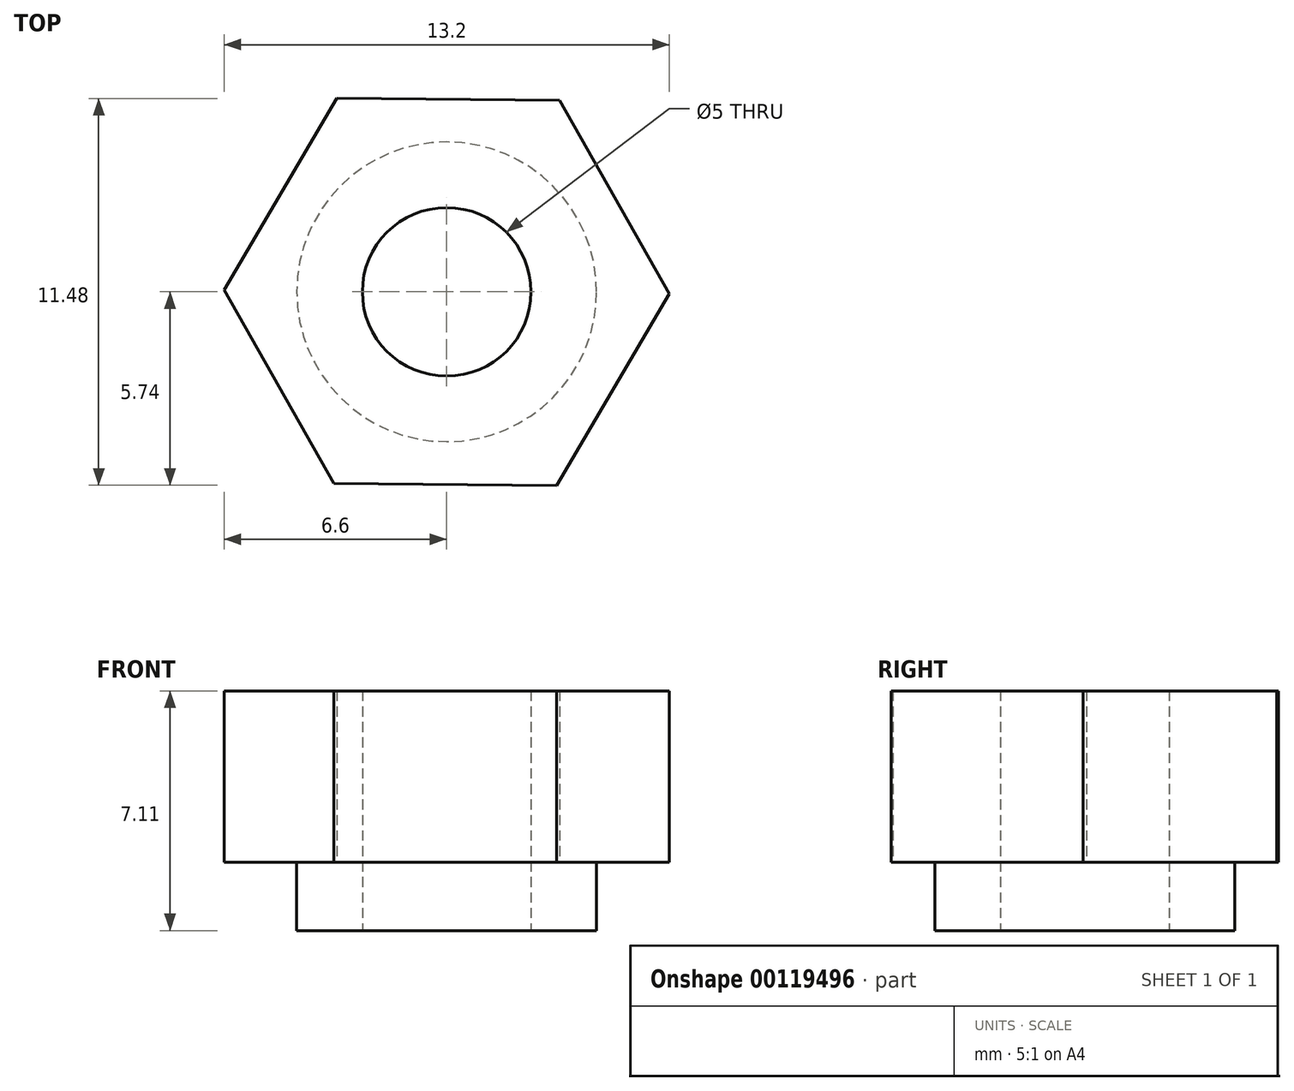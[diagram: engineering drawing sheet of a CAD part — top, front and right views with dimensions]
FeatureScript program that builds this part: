
annotation { "Feature Type Name" : "Feature", "Feature Type Description" : "" }
export const myFeature = defineFeature(function(context is Context, id is Id, definition is map)
    precondition{}
    {
        {
            var Q0;
            Q0=qCreatedBy(makeId("Top.planeOp"),FACE);
            var sketch = newSketch(context, id + "F0", { "sketchPlane" : qUnion([Q0])});
            skCircle(sketch, "E0.cCircle", {"center": v(0, 0) * mm, "radius": 6.6 * mm, "construction": true});
            skLineSegment(sketch, "E0.0", {"start": v(-3.25, 5.74) * mm, "end": v(3.35, 5.69) * mm});
            skLineSegment(sketch, "E0.1", {"start": v(3.35, 5.69) * mm, "end": v(6.6, -0.05) * mm});
            skLineSegment(sketch, "E0.2", {"start": v(6.6, -0.05) * mm, "end": v(3.25, -5.74) * mm});
            skLineSegment(sketch, "E0.3", {"start": v(3.25, -5.74) * mm, "end": v(-3.35, -5.69) * mm});
            skLineSegment(sketch, "E0.4", {"start": v(-3.35, -5.69) * mm, "end": v(-6.6, 0.05) * mm});
            skLineSegment(sketch, "E0.5", {"start": v(-6.6, 0.05) * mm, "end": v(-3.25, 5.74) * mm});
            skSolve(sketch);
        }
        {
            var Q0;
            Q0=makeQuery(id+"F0.imprint","IMPRINT",FACE,{"disambiguationData":[TD([[makeQuery(id+"F0.imprint","IMPRINT",EDGE,{"derivedFrom":sQuery(id+"F0.wireOp",EDGE,"E0.0")}),-1.0]])]});
            extrude(context, id + "F1", {"entities" : qUnion([Q0]), "depth" : 5.08 * mm});
        }
        {
            var Q0;
            Q0=makeQuery(id+"F1.opExtrude","CAP_FACE",FACE,{"disambiguationData":[OSD([sQuery(id+"F0.wireOp",EDGE,"E0.0"),sQuery(id+"F0.wireOp",EDGE,"E0.1"),sQuery(id+"F0.wireOp",EDGE,"E0.2"),sQuery(id+"F0.wireOp",EDGE,"E0.3"),sQuery(id+"F0.wireOp",EDGE,"E0.4"),sQuery(id+"F0.wireOp",EDGE,"E0.5")])],"isStart":true});
            var sketch = newSketch(context, id + "F2", { "sketchPlane" : qUnion([Q0])});
            skCircle(sketch, "E1", {"center": v(0, 0) * mm, "radius": 4.45 * mm});
            skSolve(sketch);
        }
        {
            var Q0;
            Q0 = qSketchRegion(id + "F2", true);
            var Q1;
            Q1=sQuery(id+"F2.wireOp",EDGE,"E1");
            extrude(context, id + "F3", {"entities" : qUnion([Q0]), "operationType" : NewBodyOperationType.ADD, "surfaceEntities" : qUnion([Q1]), "depth" : 2.03 * mm});
        }
        {
            var Q0;
            Q0=makeQuery(id+"F3.opExtrude","CAP_FACE",FACE,{"disambiguationData":[OSD([sQuery(id+"F2.wireOp",EDGE,"E1")])],"isStart":false});
            var sketch = newSketch(context, id + "F4", { "sketchPlane" : qUnion([Q0])});
            skPoint(sketch, "E2", {"position": v(0, 0) * mm});
            skSolve(sketch);
        }
        {
            var Q0;
            Q0=sQuery(id+"F4.wireOp",VERTEX,"E2");
            var Q1;
            Q1=makeQuery(id+"F1.opExtrude","SWEPT_BODY",BODY,{"disambiguationData":[OSD([sQuery(id+"F0.wireOp",EDGE,"E0.0"),sQuery(id+"F0.wireOp",EDGE,"E0.1"),sQuery(id+"F0.wireOp",EDGE,"E0.2"),sQuery(id+"F0.wireOp",EDGE,"E0.3"),sQuery(id+"F0.wireOp",EDGE,"E0.4"),sQuery(id+"F0.wireOp",EDGE,"E0.5")])]});
            hole(context, id + "F5", {"style" : HoleStyle.SIMPLE, "endStyle" : HoleEndStyle.THROUGH, "standardTappedOrClearance" : lookupTablePath({ "standard" : "ISO", "engagement" : "75%", "pitch" : "1 mm", "size" : "M6", "type" : "Tapped" }), "standardBlindInLast" : lookupTablePath({ "standard" : "ISO", "engagement" : "75%", "pitch" : "1 mm", "size" : "M6", "type" : "Tapped" }), "holeDiameter" : 5 * mm, "locations" : qUnion([Q0]), "scope" : qUnion([Q1]), "isTappedThrough" : true, "majorDiameter" : 6 * mm, "showTappedDepth" : true});
        }
    });
